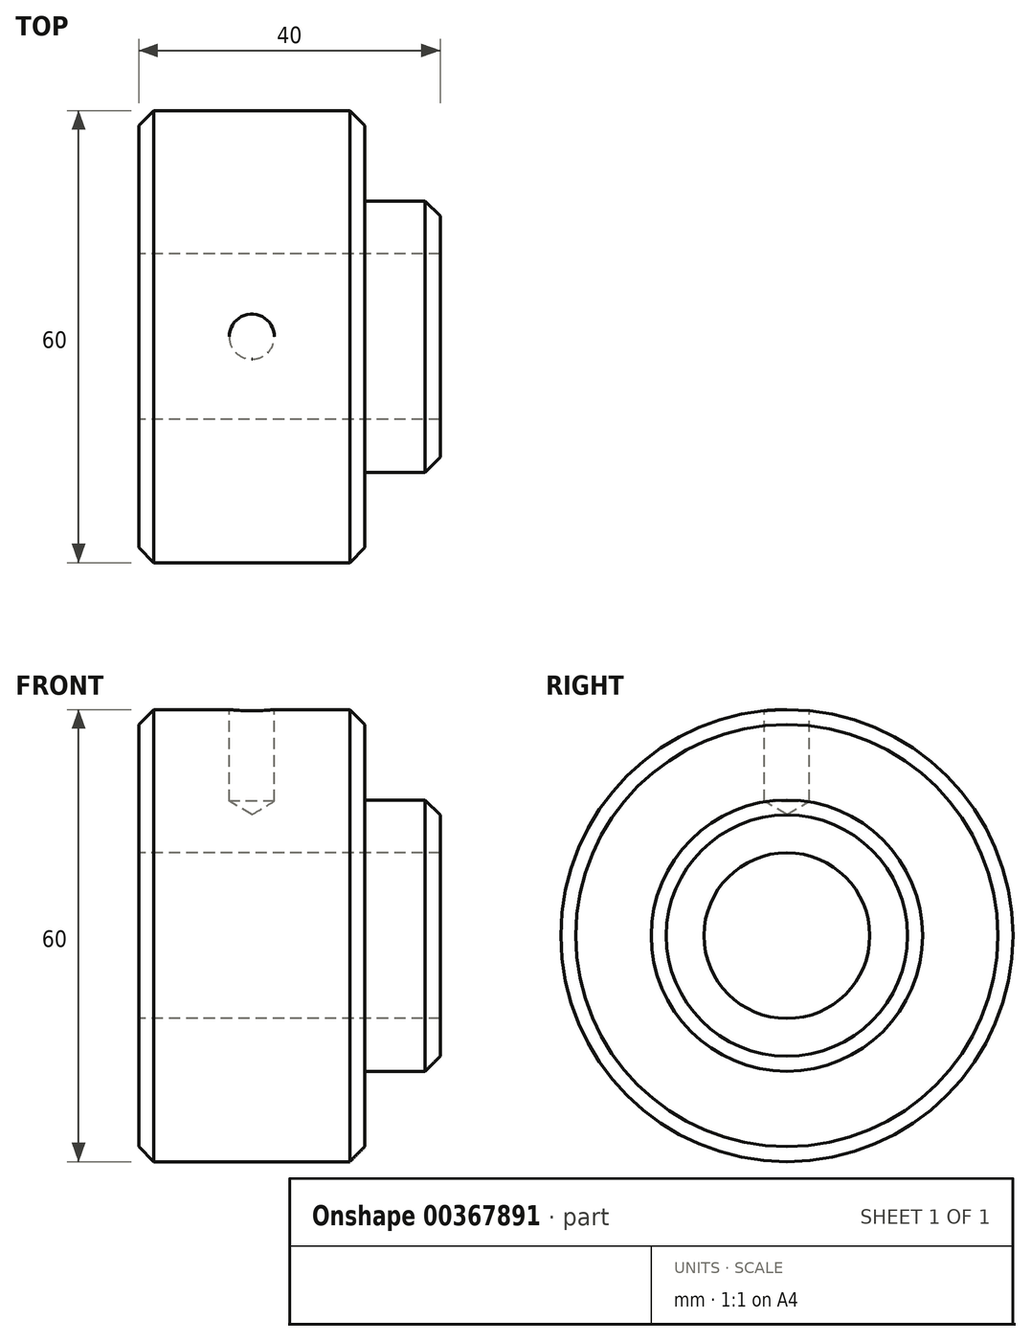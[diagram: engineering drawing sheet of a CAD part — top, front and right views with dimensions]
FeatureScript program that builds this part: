
annotation { "Feature Type Name" : "Feature", "Feature Type Description" : "" }
export const myFeature = defineFeature(function(context is Context, id is Id, definition is map)
    precondition{}
    {
        {
            var Q0;
            Q0=qCreatedBy(makeId("Front.planeOp"),FACE);
            var sketch = newSketch(context, id + "F0", { "sketchPlane" : qUnion([Q0])});
            skLineSegment(sketch, "E0", {"start": v(-30, 30) * mm, "end": v(0, 30) * mm});
            skLineSegment(sketch, "E1", {"start": v(0, 30) * mm, "end": v(0, 18) * mm});
            skLineSegment(sketch, "E2", {"start": v(0, 18) * mm, "end": v(10, 18) * mm});
            skLineSegment(sketch, "E3", {"start": v(10, 18) * mm, "end": v(10, 11) * mm});
            skLineSegment(sketch, "E4", {"start": v(10, 11) * mm, "end": v(-30, 11) * mm});
            skLineSegment(sketch, "E5", {"start": v(-30, 11) * mm, "end": v(-30, 30) * mm});
            skLineSegment(sketch, "E6", {"start": v(-74.58, 0) * mm, "end": v(74.58, 0) * mm, "construction": true});
            skSolve(sketch);
        }
        {
            var Q0;
            Q0=makeQuery(id+"F0.imprint","IMPRINT",FACE,{"disambiguationData":[TD([[makeQuery(id+"F0.imprint","IMPRINT",EDGE,{"derivedFrom":sQuery(id+"F0.wireOp",EDGE,"E0")}),-1.0]])]});
            var Q1;
            Q1=sQuery(id+"F0.wireOp",EDGE,"E6");
            revolve(context, id + "F1", {"entities" : qUnion([Q0]), "axis" : qUnion([Q1]), "revolveType" : RevolveType.FULL});
        }
        {
            var Q0;
            Q0=makeQuery(id+"F1.opRevolve","SWEPT_EDGE",EDGE,{"disambiguationData":[OSD([sQuery(id+"F0.wireOp",EDGE,"E0"),sQuery(id+"F0.wireOp",EDGE,"E1")])]});
            var Q1;
            Q1=makeQuery(id+"F1.opRevolve","SWEPT_FACE",FACE,{"disambiguationData":[OSD([sQuery(id+"F0.wireOp",EDGE,"E0")])]});
            var Q2;
            Q2=makeQuery(id+"F1.opRevolve","SWEPT_EDGE",EDGE,{"disambiguationData":[OSD([sQuery(id+"F0.wireOp",EDGE,"E2"),sQuery(id+"F0.wireOp",EDGE,"E3")])]});
            chamfer(context, id + "F2", {"entities" : qUnion([Q0, Q1, Q2]), "width" : 2 * mm, "tangentPropagation" : true});
        }
        {
            var Q0;
            Q0=qCreatedBy(makeId("Top.planeOp"),FACE);
            cPlane(context, id + "F3", {"entities" : qUnion([Q0]), "cplaneType" : CPlaneType.OFFSET, "offset" : 30 * mm, "width" : 150 * mm, "height" : 150 * mm});
        }
        {
            var Q0;
            Q0=qCreatedBy(id+"F3.planeOp",FACE);
            var sketch = newSketch(context, id + "F4", { "sketchPlane" : qUnion([Q0])});
            skCircle(sketch, "E7", {"center": v(-15, 0) * mm, "radius": 3 * mm});
            skSolve(sketch);
        }
        {
            var Q0;
            Q0=sQuery(id+"F4.wireOp",VERTEX,"E7.center");
            var Q1;
            Q1=makeQuery(id+"F1.opRevolve","SWEPT_BODY",BODY,{"disambiguationData":[OSD([sQuery(id+"F0.wireOp",EDGE,"E0"),sQuery(id+"F0.wireOp",EDGE,"E1"),sQuery(id+"F0.wireOp",EDGE,"E2"),sQuery(id+"F0.wireOp",EDGE,"E3"),sQuery(id+"F0.wireOp",EDGE,"E4"),sQuery(id+"F0.wireOp",EDGE,"E5")])]});
            hole(context, id + "F5", {"style" : HoleStyle.SIMPLE, "endStyle" : HoleEndStyle.BLIND, "holeDiameter" : 6 * mm, "holeDepth" : 12 * mm, "isTappedThrough" : true, "tappedDepth" : 12 * mm, "tapClearance" : 3, "locations" : qUnion([Q0]), "scope" : qUnion([Q1])});
        }
    });
